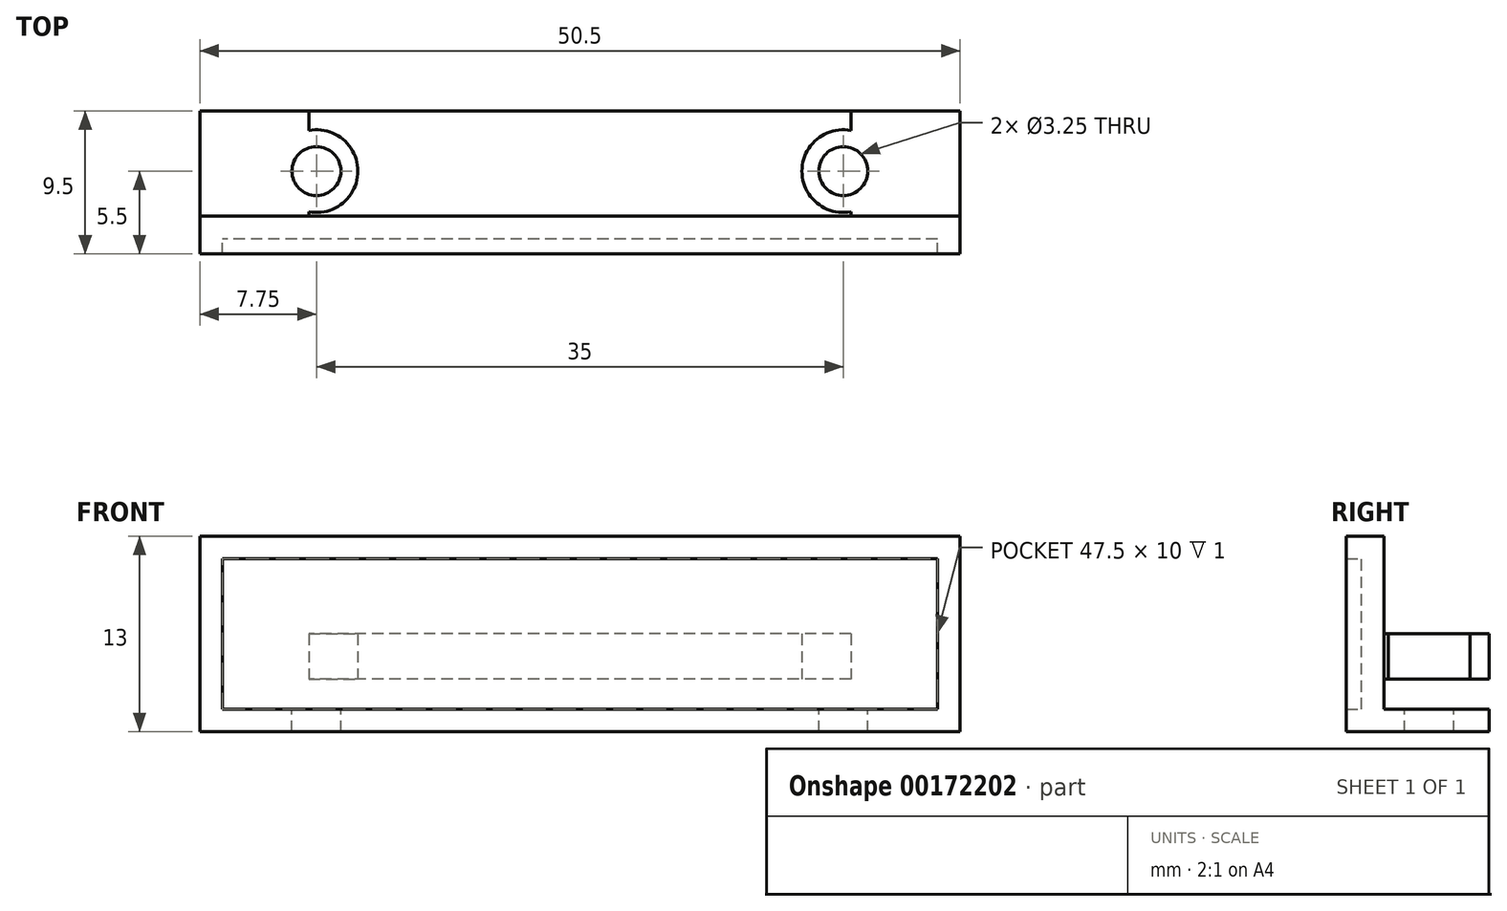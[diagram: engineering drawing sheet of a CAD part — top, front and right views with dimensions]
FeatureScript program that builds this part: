
annotation { "Feature Type Name" : "Feature", "Feature Type Description" : "" }
export const myFeature = defineFeature(function(context is Context, id is Id, definition is map)
    precondition{}
    {
        {
            var Q0;
            Q0=qCreatedBy(makeId("Top.planeOp"),FACE);
            var sketch = newSketch(context, id + "F0", { "sketchPlane" : qUnion([Q0])});
            skCircle(sketch, "E0", {"center": v(17.5, 0) * mm, "radius": 2.75 * mm});
            skCircle(sketch, "E1", {"center": v(-17.5, 0) * mm, "radius": 2.75 * mm});
            skSolve(sketch);
        }
        {
            var Q0;
            Q0=qCreatedBy(makeId("Front.planeOp"),FACE);
            cPlane(context, id + "F1", {"entities" : qUnion([Q0]), "cplaneType" : CPlaneType.OFFSET, "offset" : 3 * mm, "width" : 150 * mm, "height" : 150 * mm});
        }
        {
            var Q0;
            Q0=qCreatedBy(id+"F1.planeOp",FACE);
            var sketch = newSketch(context, id + "F2", { "sketchPlane" : qUnion([Q0])});
            skLineSegment(sketch, "E2.bottom", {"start": v(23.75, -2) * mm, "end": v(-23.75, -2) * mm});
            skLineSegment(sketch, "E2.top", {"start": v(23.75, 8) * mm, "end": v(-23.75, 8) * mm});
            skLineSegment(sketch, "E2.left", {"start": v(23.75, -2) * mm, "end": v(23.75, 8) * mm});
            skLineSegment(sketch, "E2.right", {"start": v(-23.75, -2) * mm, "end": v(-23.75, 8) * mm});
            skPoint(sketch, "E2.middle", {"position": v(0, 3) * mm});
            skLineSegment(sketch, "E3.0", {"start": v(25.25, 9.5) * mm, "end": v(-25.25, 9.5) * mm});
            skLineSegment(sketch, "E3.1", {"start": v(25.25, -3.5) * mm, "end": v(25.25, 9.5) * mm});
            skLineSegment(sketch, "E3.2", {"start": v(25.25, -3.5) * mm, "end": v(-25.25, -3.5) * mm});
            skLineSegment(sketch, "E3.3", {"start": v(-25.25, -3.5) * mm, "end": v(-25.25, 9.5) * mm});
            skSolve(sketch);
        }
        {
            var Q0;
            Q0=makeQuery(id+"F2.imprint","IMPRINT",FACE,{"disambiguationData":[TD([[makeQuery(id+"F2.imprint","IMPRINT",EDGE,{"derivedFrom":sQuery(id+"F2.wireOp",EDGE,"E2.bottom")}),1.0]])]});
            extrude(context, id + "F3", {"entities" : qUnion([Q0]), "depth" : 2.5 * mm});
        }
        {
            var Q0;
            Q0=makeQuery(id+"F2.imprint","IMPRINT",FACE,{"disambiguationData":[TD([[makeQuery(id+"F2.imprint","IMPRINT",EDGE,{"derivedFrom":sQuery(id+"F2.wireOp",EDGE,"E2.bottom")}),-1.0]])]});
            extrude(context, id + "F4", {"entities" : qUnion([Q0]), "operationType" : NewBodyOperationType.ADD, "depth" : 1.5 * mm});
        }
        {
            var Q0;
            {var subQ0=sQuery(id+"F2.wireOp",EDGE,"E2.right");var subQ1=sQuery(id+"F2.wireOp",EDGE,"E2.left");var subQ2=sQuery(id+"F2.wireOp",EDGE,"E2.top");var subQ3=sQuery(id+"F2.wireOp",EDGE,"E2.bottom");Q0=makeQuery(id+"F4.boolean.opBoolean","MERGE",FACE,{"derivedFrom":[makeQuery(id+"F3.opExtrude","CAP_FACE",FACE,{"disambiguationData":[OSD([subQ3,subQ2,subQ1,subQ0,sQuery(id+"F2.wireOp",EDGE,"E3.0"),sQuery(id+"F2.wireOp",EDGE,"E3.1"),sQuery(id+"F2.wireOp",EDGE,"E3.2"),sQuery(id+"F2.wireOp",EDGE,"E3.3")])],"isStart":true}),makeQuery(id+"F4.opExtrude","CAP_FACE",FACE,{"disambiguationData":[OSD([subQ3,subQ2,subQ1,subQ0])],"isStart":true})]});}
            var sketch = newSketch(context, id + "F5", { "sketchPlane" : qUnion([Q0])});
            skLineSegment(sketch, "E4.bottom", {"start": v(-18, 3) * mm, "end": v(18, 3) * mm});
            skLineSegment(sketch, "E4.top", {"start": v(-18, 0) * mm, "end": v(18, 0) * mm});
            skLineSegment(sketch, "E4.left", {"start": v(-18, 3) * mm, "end": v(-18, 0) * mm});
            skLineSegment(sketch, "E4.right", {"start": v(18, 3) * mm, "end": v(18, 0) * mm});
            skLineSegment(sketch, "E5.bottom", {"start": v(25.25, -3.5) * mm, "end": v(-25.25, -3.5) * mm});
            skLineSegment(sketch, "E5.top", {"start": v(25.25, -2) * mm, "end": v(-25.25, -2) * mm});
            skLineSegment(sketch, "E5.left", {"start": v(25.25, -3.5) * mm, "end": v(25.25, -2) * mm});
            skLineSegment(sketch, "E5.right", {"start": v(-25.25, -3.5) * mm, "end": v(-25.25, -2) * mm});
            skSolve(sketch);
        }
        {
            var Q0;
            Q0 = qSketchRegion(id + "F5", true);
            extrude(context, id + "F6", {"entities" : qUnion([Q0]), "operationType" : NewBodyOperationType.ADD, "depth" : 7 * mm});
        }
        {
            var Q0;
            Q0 = qSketchRegion(id + "F0", true);
            extrude(context, id + "F7", {"entities" : qUnion([Q0]), "operationType" : NewBodyOperationType.REMOVE, "depth" : 25 * mm});
        }
        {
            var Q0;
            Q0=qCreatedBy(makeId("Top.planeOp"),FACE);
            var sketch = newSketch(context, id + "F8", { "sketchPlane" : qUnion([Q0])});
            skCircle(sketch, "E6", {"center": v(-17.5, 0) * mm, "radius": 1.63 * mm});
            skCircle(sketch, "E7", {"center": v(17.5, 0) * mm, "radius": 1.63 * mm});
            skSolve(sketch);
        }
        {
            var Q0;
            Q0 = qSketchRegion(id + "F8", true);
            extrude(context, id + "F9", {"entities" : qUnion([Q0]), "operationType" : NewBodyOperationType.REMOVE, "endBound" : BoundingType.THROUGH_ALL, "oppositeDirection" : true, "depth" : 25 * mm});
        }
    });
